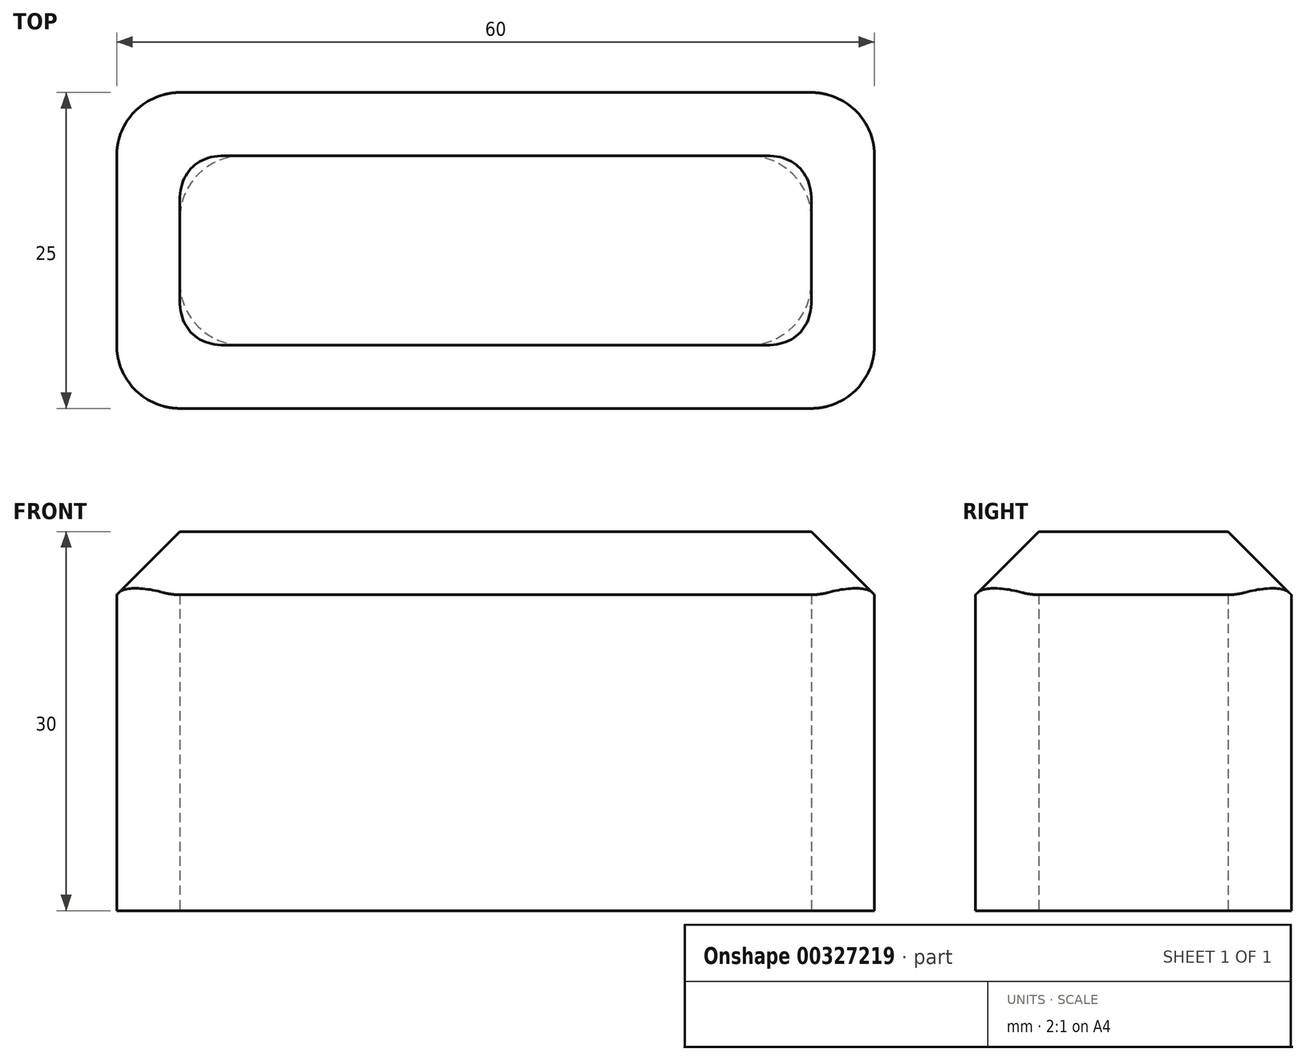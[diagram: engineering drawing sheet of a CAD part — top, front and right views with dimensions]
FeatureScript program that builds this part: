
annotation { "Feature Type Name" : "Feature", "Feature Type Description" : "" }
export const myFeature = defineFeature(function(context is Context, id is Id, definition is map)
    precondition{}
    {
        {
            var Q0;
            Q0=qCreatedBy(makeId("Top.planeOp"),FACE);
            var sketch = newSketch(context, id + "F0", { "sketchPlane" : qUnion([Q0])});
            skLineSegment(sketch, "E0.bottom", {"start": v(-30, -12.5) * mm, "end": v(30, -12.5) * mm});
            skLineSegment(sketch, "E0.top", {"start": v(-30, 12.5) * mm, "end": v(30, 12.5) * mm});
            skLineSegment(sketch, "E0.left", {"start": v(-30, -12.5) * mm, "end": v(-30, 12.5) * mm});
            skLineSegment(sketch, "E0.right", {"start": v(30, -12.5) * mm, "end": v(30, 12.5) * mm});
            skPoint(sketch, "E0.middle", {"position": v(0, 0) * mm});
            skSolve(sketch);
        }
        {
            var Q0;
            Q0=makeQuery(id+"F0.imprint","IMPRINT",FACE,{"disambiguationData":[TD([[makeQuery(id+"F0.imprint","IMPRINT",EDGE,{"derivedFrom":sQuery(id+"F0.wireOp",EDGE,"E0.bottom")}),1.0]])]});
            extrude(context, id + "F1", {"entities" : qUnion([Q0]), "depth" : 30 * mm});
        }
        {
            var Q0;
            Q0=makeQuery(id+"F1.opExtrude","CAP_FACE",FACE,{"disambiguationData":[OSD([sQuery(id+"F0.wireOp",EDGE,"E0.bottom"),sQuery(id+"F0.wireOp",EDGE,"E0.top"),sQuery(id+"F0.wireOp",EDGE,"E0.left"),sQuery(id+"F0.wireOp",EDGE,"E0.right")])],"isStart":false});
            chamfer(context, id + "F2", {"entities" : qUnion([Q0]), "width" : 5 * mm, "tangentPropagation" : true});
        }
        {
            var Q0;
            Q0=makeQuery(id+"F1.opExtrude","SWEPT_EDGE",EDGE,{"disambiguationData":[OSD([sQuery(id+"F0.wireOp",EDGE,"E0.bottom"),sQuery(id+"F0.wireOp",EDGE,"E0.left")])]});
            var Q1;
            Q1=makeQuery(id+"F1.opExtrude","SWEPT_EDGE",EDGE,{"disambiguationData":[OSD([sQuery(id+"F0.wireOp",EDGE,"E0.bottom"),sQuery(id+"F0.wireOp",EDGE,"E0.right")])]});
            var Q2;
            Q2=makeQuery(id+"F1.opExtrude","SWEPT_EDGE",EDGE,{"disambiguationData":[OSD([sQuery(id+"F0.wireOp",EDGE,"E0.top"),sQuery(id+"F0.wireOp",EDGE,"E0.right")])]});
            var Q3;
            Q3=makeQuery(id+"F1.opExtrude","SWEPT_EDGE",EDGE,{"disambiguationData":[OSD([sQuery(id+"F0.wireOp",EDGE,"E0.top"),sQuery(id+"F0.wireOp",EDGE,"E0.left")])]});
            var Q4;
            Q4=makeQuery(id+"F2.opChamfer","BLEND_EDGE",EDGE,{"blendedFrom":[makeQuery(id+"F1.opExtrude","CAP_EDGE",EDGE,{"disambiguationData":[OSD([sQuery(id+"F0.wireOp",EDGE,"E0.top")])],"isStart":false}),makeQuery(id+"F1.opExtrude","CAP_EDGE",EDGE,{"disambiguationData":[OSD([sQuery(id+"F0.wireOp",EDGE,"E0.left")])],"isStart":false})],"blendedInto":[]});
            var Q5;
            Q5=makeQuery(id+"F2.opChamfer","BLEND_EDGE",EDGE,{"blendedFrom":[makeQuery(id+"F1.opExtrude","CAP_EDGE",EDGE,{"disambiguationData":[OSD([sQuery(id+"F0.wireOp",EDGE,"E0.top")])],"isStart":false}),makeQuery(id+"F1.opExtrude","CAP_EDGE",EDGE,{"disambiguationData":[OSD([sQuery(id+"F0.wireOp",EDGE,"E0.right")])],"isStart":false})],"blendedInto":[]});
            var Q6;
            Q6=makeQuery(id+"F2.opChamfer","BLEND_EDGE",EDGE,{"blendedFrom":[makeQuery(id+"F1.opExtrude","CAP_EDGE",EDGE,{"disambiguationData":[OSD([sQuery(id+"F0.wireOp",EDGE,"E0.bottom")])],"isStart":false}),makeQuery(id+"F1.opExtrude","CAP_EDGE",EDGE,{"disambiguationData":[OSD([sQuery(id+"F0.wireOp",EDGE,"E0.right")])],"isStart":false})],"blendedInto":[]});
            var Q7;
            Q7=makeQuery(id+"F2.opChamfer","BLEND_EDGE",EDGE,{"blendedFrom":[makeQuery(id+"F1.opExtrude","CAP_EDGE",EDGE,{"disambiguationData":[OSD([sQuery(id+"F0.wireOp",EDGE,"E0.bottom")])],"isStart":false}),makeQuery(id+"F1.opExtrude","CAP_EDGE",EDGE,{"disambiguationData":[OSD([sQuery(id+"F0.wireOp",EDGE,"E0.left")])],"isStart":false})],"blendedInto":[]});
            fillet(context, id + "F3", {"entities" : qUnion([Q0, Q1, Q2, Q3, Q4, Q5, Q6, Q7]), "radius" : 5 * mm, "tangentPropagation" : true, "allowEdgeOverflow" : false});
        }
        {
            var Q0;
            Q0=makeQuery(id+"F1.opExtrude","CAP_FACE",FACE,{"disambiguationData":[OSD([sQuery(id+"F0.wireOp",EDGE,"E0.bottom"),sQuery(id+"F0.wireOp",EDGE,"E0.top"),sQuery(id+"F0.wireOp",EDGE,"E0.left"),sQuery(id+"F0.wireOp",EDGE,"E0.right")])],"isStart":true});
            var sketch = newSketch(context, id + "F4", { "sketchPlane" : qUnion([Q0])});
            skLineSegment(sketch, "E1.bottom", {"start": v(-20, -7.5) * mm, "end": v(20, -7.5) * mm});
            skLineSegment(sketch, "E1.top", {"start": v(-20, 7.5) * mm, "end": v(20, 7.5) * mm});
            skLineSegment(sketch, "E1.left", {"start": v(-25, -2.5) * mm, "end": v(-25, 2.5) * mm});
            skLineSegment(sketch, "E1.right", {"start": v(25, -2.5) * mm, "end": v(25, 2.5) * mm});
            skPoint(sketch, "E1.middle", {"position": v(0, 0) * mm});
            skPoint(sketch, "E2.visualSharp", {"position": v(-25, 7.5) * mm});
            skArc(sketch, "E2.filletArc", {"start": v(-20, 7.5) * mm, "mid": v(-23.54, 6.04) * mm, "end": v(-25, 2.5) * mm});
            skPoint(sketch, "E3.visualSharp", {"position": v(-25, -7.5) * mm});
            skArc(sketch, "E3.filletArc", {"start": v(-25, -2.5) * mm, "mid": v(-23.54, -6.04) * mm, "end": v(-20, -7.5) * mm});
            skPoint(sketch, "E4.visualSharp", {"position": v(25, -7.5) * mm});
            skArc(sketch, "E4.filletArc", {"start": v(20, -7.5) * mm, "mid": v(23.54, -6.04) * mm, "end": v(25, -2.5) * mm});
            skPoint(sketch, "E5.visualSharp", {"position": v(25, 7.5) * mm});
            skArc(sketch, "E5.filletArc", {"start": v(25, 2.5) * mm, "mid": v(23.54, 6.04) * mm, "end": v(20, 7.5) * mm});
            skSolve(sketch);
        }
        {
            var Q0;
            Q0 = qSketchRegion(id + "F4", true);
            extrude(context, id + "F5", {"entities" : qUnion([Q0]), "operationType" : NewBodyOperationType.REMOVE, "oppositeDirection" : true, "depth" : 25 * mm});
        }
    });
